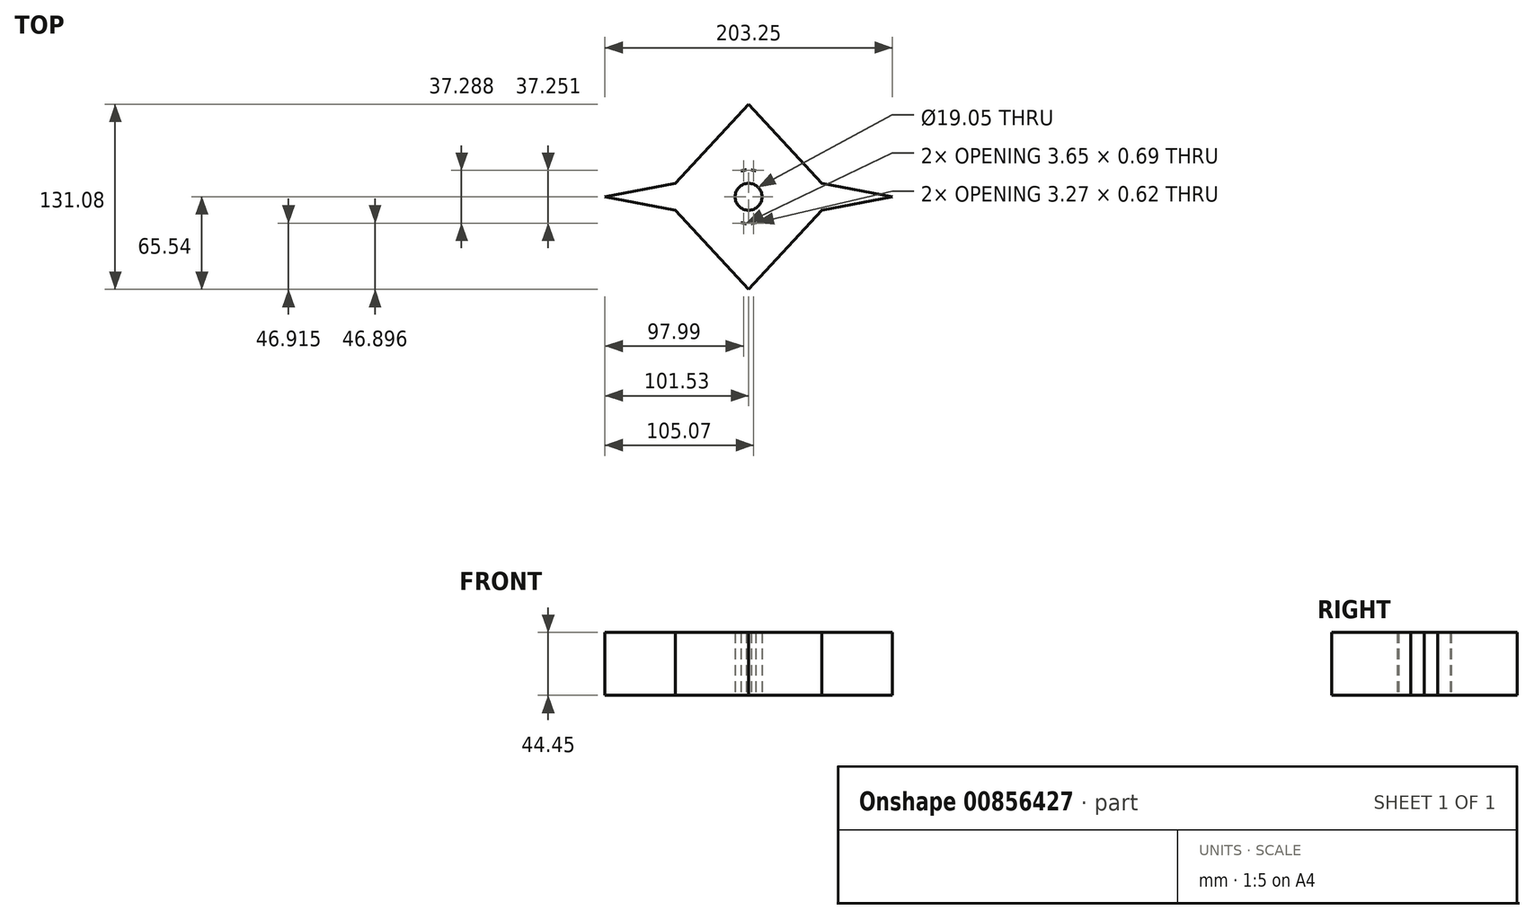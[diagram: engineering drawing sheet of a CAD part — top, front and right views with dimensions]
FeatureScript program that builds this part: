
annotation { "Feature Type Name" : "Feature", "Feature Type Description" : "" }
export const myFeature = defineFeature(function(context is Context, id is Id, definition is map)
    precondition{}
    {
        {
            var Q0;
            Q0=qCreatedBy(makeId("Top.planeOp"),FACE);
            var sketch = newSketch(context, id + "F0", { "sketchPlane" : qUnion([Q0])});
            skCircle(sketch, "E0", {"center": v(0, 0) * mm, "radius": 19.05 * mm});
            skCircle(sketch, "E1", {"center": v(0, 0) * mm, "radius": 9.53 * mm});
            skLineSegment(sketch, "E2", {"start": v(1.9, -18.95) * mm, "end": v(101.72, 0) * mm});
            skLineSegment(sketch, "E3", {"start": v(1.9, 18.95) * mm, "end": v(101.72, 0) * mm});
            skLineSegment(sketch, "E4", {"start": v(-1.71, 18.97) * mm, "end": v(-101.53, 0) * mm});
            skLineSegment(sketch, "E5", {"start": v(-1.71, -18.97) * mm, "end": v(-101.53, 0) * mm});
            skLineSegment(sketch, "E6", {"start": v(-1.71, -18.97) * mm, "end": v(0, -65.54) * mm});
            skLineSegment(sketch, "E7", {"start": v(1.9, -18.95) * mm, "end": v(0, -65.54) * mm});
            skLineSegment(sketch, "E8", {"start": v(-1.71, 18.97) * mm, "end": v(0, 65.54) * mm});
            skLineSegment(sketch, "E9", {"start": v(1.9, 18.95) * mm, "end": v(0, 65.54) * mm});
            skLineSegment(sketch, "E10", {"start": v(0, -65.54) * mm, "end": v(-51.62, -9.49) * mm});
            skLineSegment(sketch, "E11", {"start": v(0, -65.54) * mm, "end": v(51.64, -9.5) * mm});
            skLineSegment(sketch, "E12", {"start": v(0, 65.54) * mm, "end": v(-51.62, 9.49) * mm});
            skLineSegment(sketch, "E13", {"start": v(0, 65.54) * mm, "end": v(51.64, 9.5) * mm});
            skSolve(sketch);
        }
        {
            var Q0;
            Q0=makeQuery(id+"F0.imprint","IMPRINT",FACE,{"disambiguationData":[TD([[makeQuery(id+"F0.imprint","IMPRINT",EDGE,{"derivedFrom":sQuery(id+"F0.wireOp",EDGE,"E0")}),1.0]])]});
            extrude(context, id + "F1", {"entities" : qUnion([Q0]), "depth" : 44.45 * mm, "offsetDistance" : 25.4 * mm});
        }
        {
            var Q0;
            {var subQ0=sQuery(id+"F0.wireOp",EDGE,"E3");var subQ1=sQuery(id+"F0.wireOp",EDGE,"E0");var subQ2=makeQuery(id+"F0.imprint","INTERSECT",VERTEX,{"disambiguationData":[OD(1.0)],"derivedFrom":[subQ1,subQ0]});Q0=makeQuery(id+"F0.imprint","IMPRINT",FACE,{"disambiguationData":[TD([[makeQuery(id+"F0.imprint","IMPRINT",EDGE,{"disambiguationData":[TD([[subQ2,1.0]])],"derivedFrom":subQ1}),-1.0]])]});}
            extrude(context, id + "F2", {"entities" : qUnion([Q0]), "operationType" : NewBodyOperationType.ADD, "depth" : 44.45 * mm, "offsetDistance" : 25.4 * mm});
        }
        {
            var Q0;
            {var subQ0=sQuery(id+"F0.wireOp",EDGE,"E4");var subQ1=sQuery(id+"F0.wireOp",EDGE,"E0");var subQ2=makeQuery(id+"F0.imprint","INTERSECT",VERTEX,{"disambiguationData":[OD(1.0)],"derivedFrom":[subQ1,subQ0]});Q0=makeQuery(id+"F0.imprint","IMPRINT",FACE,{"disambiguationData":[TD([[makeQuery(id+"F0.imprint","IMPRINT",EDGE,{"disambiguationData":[TD([[subQ2,-1.0]])],"derivedFrom":subQ1}),-1.0]])]});}
            extrude(context, id + "F3", {"entities" : qUnion([Q0]), "operationType" : NewBodyOperationType.ADD, "depth" : 44.45 * mm, "offsetDistance" : 25.4 * mm});
        }
        {
            var Q0;
            {var subQ2=sQuery(id+"F0.wireOp",EDGE,"E6");Q0=makeQuery(id+"F0.imprint","IMPRINT",FACE,{"disambiguationData":[TD([[makeQuery(id+"F0.imprint","IMPRINT",EDGE,{"derivedFrom":subQ2}),1.0]])]});}
            extrude(context, id + "F4", {"entities" : qUnion([Q0]), "operationType" : NewBodyOperationType.ADD, "depth" : 44.45 * mm, "offsetDistance" : 25.4 * mm});
        }
        {
            var Q0;
            {var subQ2=sQuery(id+"F0.wireOp",EDGE,"E8");Q0=makeQuery(id+"F0.imprint","IMPRINT",FACE,{"disambiguationData":[TD([[makeQuery(id+"F0.imprint","IMPRINT",EDGE,{"derivedFrom":subQ2}),-1.0]])]});}
            extrude(context, id + "F5", {"entities" : qUnion([Q0]), "operationType" : NewBodyOperationType.ADD, "depth" : 44.45 * mm, "offsetDistance" : 25.4 * mm});
        }
        {
            var Q0;
            {var subQ0=sQuery(id+"F0.wireOp",EDGE,"E6");Q0=makeQuery(id+"F0.imprint","IMPRINT",FACE,{"disambiguationData":[TD([[makeQuery(id+"F0.imprint","IMPRINT",EDGE,{"derivedFrom":subQ0}),-1.0]])]});}
            var Q1;
            {var subQ0=sQuery(id+"F0.wireOp",EDGE,"E7");Q1=makeQuery(id+"F0.imprint","IMPRINT",FACE,{"disambiguationData":[TD([[makeQuery(id+"F0.imprint","IMPRINT",EDGE,{"derivedFrom":subQ0}),1.0]])]});}
            extrude(context, id + "F6", {"entities" : qUnion([Q0, Q1]), "operationType" : NewBodyOperationType.ADD, "depth" : 44.45 * mm, "offsetDistance" : 25.4 * mm});
        }
        {
            var Q0;
            {var subQ0=sQuery(id+"F0.wireOp",EDGE,"E9");Q0=makeQuery(id+"F0.imprint","IMPRINT",FACE,{"disambiguationData":[TD([[makeQuery(id+"F0.imprint","IMPRINT",EDGE,{"derivedFrom":subQ0}),-1.0]])]});}
            extrude(context, id + "F7", {"entities" : qUnion([Q0]), "operationType" : NewBodyOperationType.ADD, "depth" : 44.45 * mm, "offsetDistance" : 25.4 * mm});
        }
        {
            var Q0;
            {var subQ0=sQuery(id+"F0.wireOp",EDGE,"E8");Q0=makeQuery(id+"F0.imprint","IMPRINT",FACE,{"disambiguationData":[TD([[makeQuery(id+"F0.imprint","IMPRINT",EDGE,{"derivedFrom":subQ0}),1.0]])]});}
            extrude(context, id + "F8", {"entities" : qUnion([Q0]), "operationType" : NewBodyOperationType.ADD, "depth" : 25.4 * mm, "offsetDistance" : 25.4 * mm});
        }
        {
            var Q0;
            Q0=makeQuery(id+"F8.opExtrude","CAP_FACE",FACE,{"disambiguationData":[OSD([sQuery(id+"F0.wireOp",EDGE,"E0"),sQuery(id+"F0.wireOp",EDGE,"E4"),sQuery(id+"F0.wireOp",EDGE,"E8"),sQuery(id+"F0.wireOp",EDGE,"E12")])],"isStart":false});
            extrude(context, id + "F9", {"entities" : qUnion([Q0]), "operationType" : NewBodyOperationType.ADD, "depth" : 19.05 * mm, "offsetDistance" : 25.4 * mm});
        }
    });
